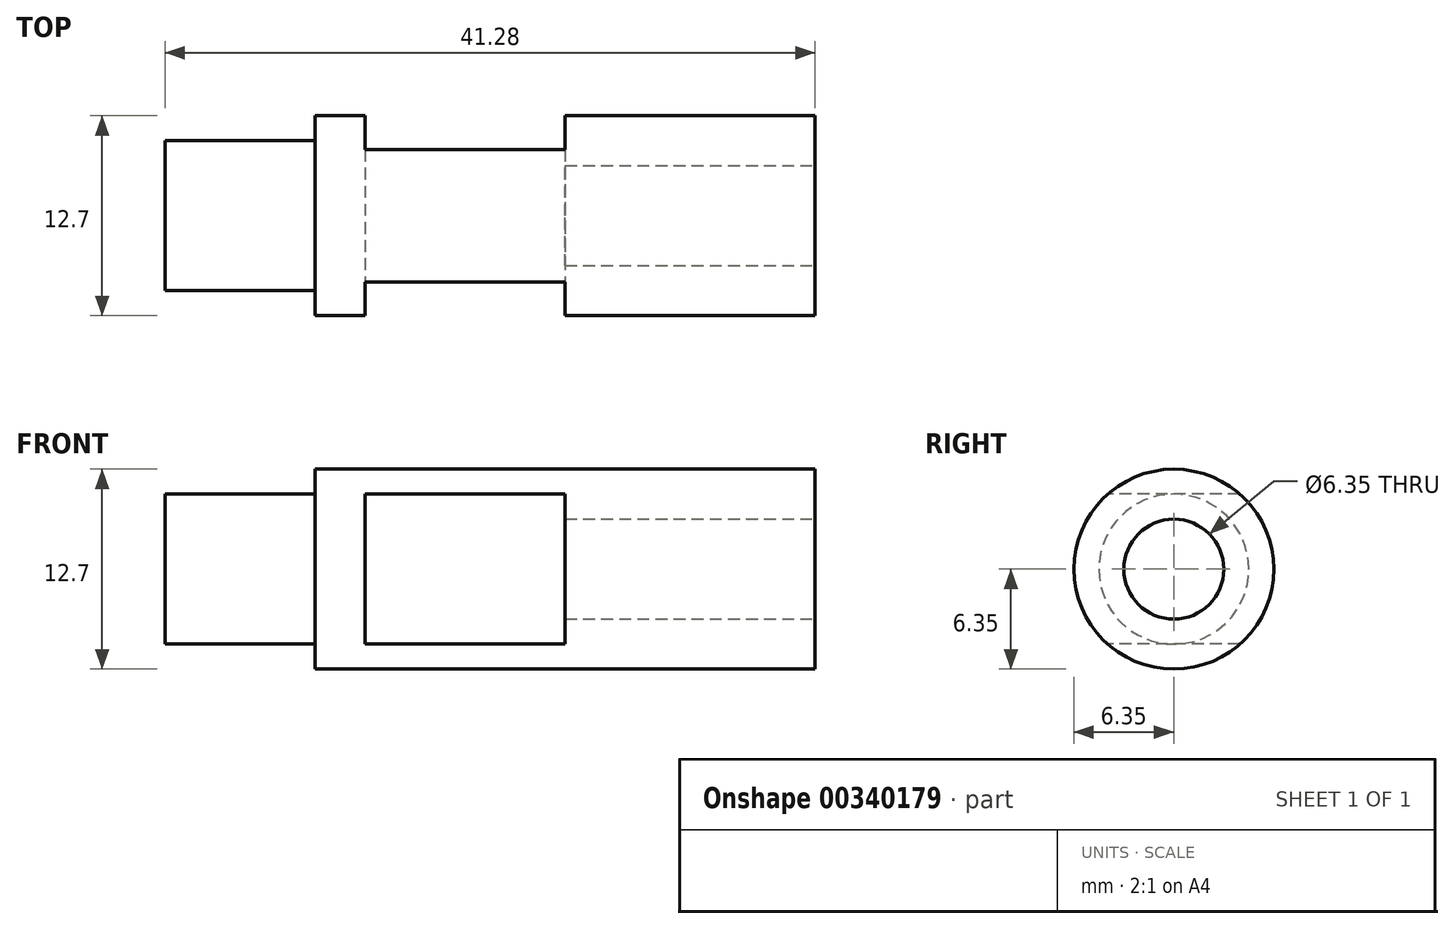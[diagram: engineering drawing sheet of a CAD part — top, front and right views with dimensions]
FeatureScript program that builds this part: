
annotation { "Feature Type Name" : "Feature", "Feature Type Description" : "" }
export const myFeature = defineFeature(function(context is Context, id is Id, definition is map)
    precondition{}
    {
        {
            var Q0;
            Q0=qCreatedBy(makeId("Front.planeOp"),FACE);
            var sketch = newSketch(context, id + "F0", { "sketchPlane" : qUnion([Q0])});
            skLineSegment(sketch, "E0", {"start": v(0, 0) * mm, "end": v(0, 4.76) * mm});
            skLineSegment(sketch, "E1", {"start": v(0, 4.76) * mm, "end": v(9.53, 4.76) * mm});
            skLineSegment(sketch, "E2", {"start": v(9.53, 4.76) * mm, "end": v(9.53, 6.35) * mm});
            skLineSegment(sketch, "E3", {"start": v(9.53, 6.35) * mm, "end": v(41.27, 6.35) * mm});
            skLineSegment(sketch, "E4", {"start": v(41.27, 6.35) * mm, "end": v(41.27, 3.18) * mm});
            skLineSegment(sketch, "E5", {"start": v(41.27, 3.18) * mm, "end": v(22.23, 3.18) * mm});
            skLineSegment(sketch, "E6", {"start": v(22.23, 3.18) * mm, "end": v(22.23, 0) * mm});
            skLineSegment(sketch, "E7", {"start": v(22.23, 0) * mm, "end": v(0, 0) * mm});
            skSolve(sketch);
        }
        {
            var Q0;
            Q0=makeQuery(id+"F0.imprint","IMPRINT",FACE,{"disambiguationData":[TD([[makeQuery(id+"F0.imprint","IMPRINT",EDGE,{"derivedFrom":sQuery(id+"F0.wireOp",EDGE,"E0")}),-1.0]])]});
            var Q1;
            Q1=sQuery(id+"F0.wireOp",EDGE,"E7");
            revolve(context, id + "F1", {"entities" : qUnion([Q0]), "axis" : qUnion([Q1]), "revolveType" : RevolveType.FULL});
        }
        {
            var Q0;
            Q0=qCreatedBy(makeId("Front.planeOp"),FACE);
            var sketch = newSketch(context, id + "F2", { "sketchPlane" : qUnion([Q0])});
            skLineSegment(sketch, "E8", {"start": v(0, 0) * mm, "end": v(41.28, 0) * mm});
            skLineSegment(sketch, "E9.bottom", {"start": v(25.4, -4.76) * mm, "end": v(12.7, -4.76) * mm});
            skLineSegment(sketch, "E9.top", {"start": v(25.4, 4.76) * mm, "end": v(12.7, 4.76) * mm});
            skLineSegment(sketch, "E9.left", {"start": v(25.4, -4.76) * mm, "end": v(25.4, 4.76) * mm});
            skLineSegment(sketch, "E9.right", {"start": v(12.7, -4.76) * mm, "end": v(12.7, 4.76) * mm});
            skPoint(sketch, "E9.middle", {"position": v(19.05, 0) * mm});
            skLineSegment(sketch, "E10", {"start": v(9.53, 4.76) * mm, "end": v(9.53, 6.35) * mm});
            skLineSegment(sketch, "E11", {"start": v(9.53, -6.35) * mm, "end": v(9.53, -4.76) * mm});
            skSolve(sketch);
        }
        {
            var Q0;
            Q0 = qSketchRegion(id + "F2", true);
            extrude(context, id + "F3", {"entities" : qUnion([Q0]), "operationType" : NewBodyOperationType.REMOVE, "endBound" : BoundingType.THROUGH_ALL, "oppositeDirection" : true, "depth" : 25.4 * mm, "hasSecondDirection" : true, "secondDirectionBound" : BoundingType.THROUGH_ALL, "secondDirectionOppositeDirection" : false, "secondDirectionDepth" : 25.4 * mm});
        }
    });
